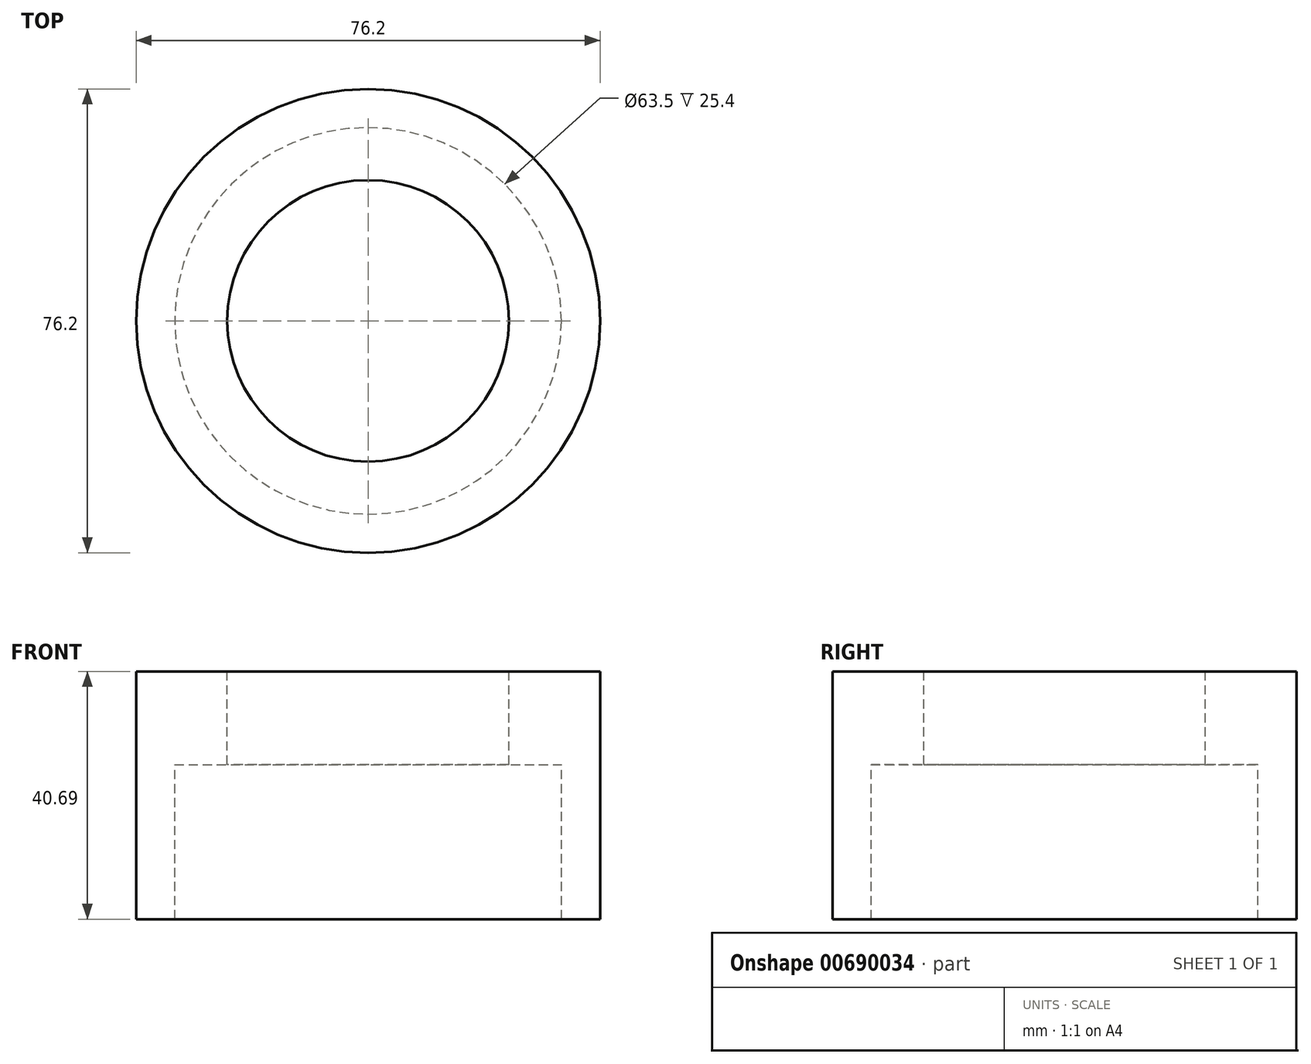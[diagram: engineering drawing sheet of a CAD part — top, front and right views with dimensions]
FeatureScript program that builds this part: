
annotation { "Feature Type Name" : "Feature", "Feature Type Description" : "" }
export const myFeature = defineFeature(function(context is Context, id is Id, definition is map)
    precondition{}
    {
        {
            var Q0;
            Q0=qCreatedBy(makeId("Top.planeOp"),FACE);
            cPlane(context, id + "F0", {"entities" : qUnion([Q0]), "cplaneType" : CPlaneType.OFFSET, "offset" : 83.28 * mm, "oppositeDirection" : true, "width" : 152.4 * mm, "height" : 152.4 * mm});
        }
        {
            var Q0;
            Q0=qCreatedBy(id+"F0.planeOp",FACE);
            var sketch = newSketch(context, id + "F1", { "sketchPlane" : qUnion([Q0])});
            skCircle(sketch, "E0", {"center": v(0, 0) * mm, "radius": 38.1 * mm});
            skSolve(sketch);
        }
        {
            var Q0;
            Q0=makeQuery(id+"F1.imprint","IMPRINT",FACE,{"disambiguationData":[TD([[makeQuery(id+"F1.imprint","IMPRINT",EDGE,{"derivedFrom":sQuery(id+"F1.wireOp",EDGE,"E0")}),1.0]])]});
            extrude(context, id + "F2", {"entities" : qUnion([Q0]), "oppositeDirection" : true, "depth" : 15.28 * mm, "offsetDistance" : 25.4 * mm});
        }
        {
            var Q0;
            Q0=makeQuery(id+"F2.opExtrude","CAP_FACE",FACE,{"disambiguationData":[OSD([sQuery(id+"F1.wireOp",EDGE,"E0")])],"isStart":true});
            var sketch = newSketch(context, id + "F3", { "sketchPlane" : qUnion([Q0])});
            skCircle(sketch, "E1", {"center": v(0, 0) * mm, "radius": 23.13 * mm});
            skSolve(sketch);
        }
        {
            var Q0;
            Q0=makeQuery(id+"F3.imprint","IMPRINT",FACE,{"disambiguationData":[TD([[makeQuery(id+"F3.imprint","IMPRINT",EDGE,{"derivedFrom":sQuery(id+"F3.wireOp",EDGE,"E1")}),1.0]])]});
            var Q1;
            Q1=makeQuery(id+"FEsZpzFsRAUAphx_14.opExtrude","CAP_FACE",FACE,{"disambiguationData":[OSD([sQuery(id+"FRgRZY7142qErhK_14.wireOp",EDGE,"07825096-29e9-43c9-bd1f-75e18fd8684c"),sQuery(id+"FRgRZY7142qErhK_14.wireOp",EDGE,"7a967d8d-9478-48be-89ff-9286eff76f60")])],"isStart":false});
            extrude(context, id + "F4", {"entities" : qUnion([Q0, Q1]), "operationType" : NewBodyOperationType.REMOVE, "oppositeDirection" : true, "depth" : 25.4 * mm, "offsetDistance" : 25.4 * mm});
        }
        {
            var Q0;
            Q0=makeQuery(id+"F2.opExtrude","CAP_FACE",FACE,{"disambiguationData":[OSD([sQuery(id+"F1.wireOp",EDGE,"E0")])],"isStart":false});
            var sketch = newSketch(context, id + "F5", { "sketchPlane" : qUnion([Q0])});
            skCircle(sketch, "E2", {"center": v(0, 0) * mm, "radius": 38.1 * mm});
            skCircle(sketch, "E3", {"center": v(0, 0) * mm, "radius": 31.75 * mm});
            skSolve(sketch);
        }
        {
            var Q0;
            Q0=makeQuery(id+"F5.imprint","IMPRINT",FACE,{"disambiguationData":[TD([[makeQuery(id+"F5.imprint","IMPRINT",EDGE,{"derivedFrom":sQuery(id+"F5.wireOp",EDGE,"E2")}),-1.0]])]});
            extrude(context, id + "F6", {"entities" : qUnion([Q0]), "operationType" : NewBodyOperationType.ADD, "depth" : 25.4 * mm, "offsetDistance" : 25.4 * mm});
        }
    });
